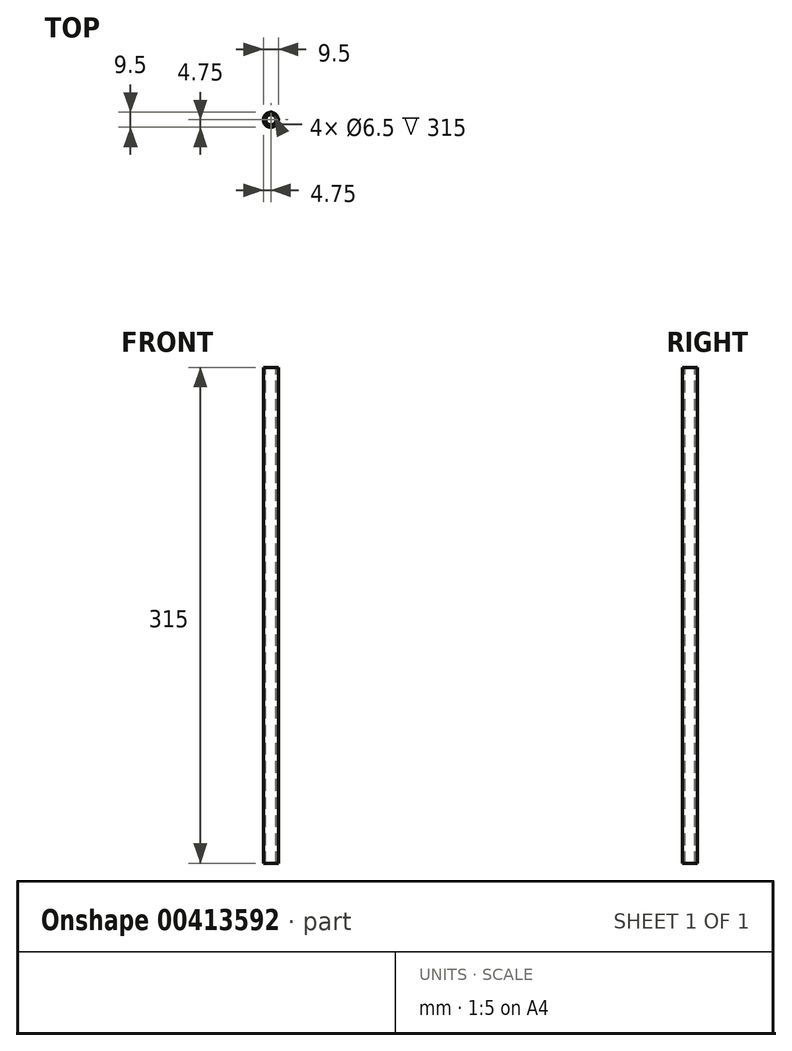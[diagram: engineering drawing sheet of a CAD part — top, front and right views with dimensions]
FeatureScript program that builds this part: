
annotation { "Feature Type Name" : "Feature", "Feature Type Description" : "" }
export const myFeature = defineFeature(function(context is Context, id is Id, definition is map)
    precondition{}
    {
        {
            var Q0;
            Q0=qCreatedBy(makeId("Front.planeOp"),FACE);
            var sketch = newSketch(context, id + "F0", { "sketchPlane" : qUnion([Q0])});
            skLineSegment(sketch, "E0.bottom", {"start": v(-3.25, -157.5) * mm, "end": v(-4.75, -157.5) * mm});
            skLineSegment(sketch, "E0.top", {"start": v(-3.25, 157.5) * mm, "end": v(-4.75, 157.5) * mm});
            skLineSegment(sketch, "E0.left", {"start": v(-3.25, -157.5) * mm, "end": v(-3.25, 157.5) * mm});
            skLineSegment(sketch, "E0.right", {"start": v(-4.75, -157.5) * mm, "end": v(-4.75, 157.5) * mm});
            skPoint(sketch, "E1", {"position": v(-3.25, 0) * mm});
            skLineSegment(sketch, "E2", {"start": v(0, 74.9) * mm, "end": v(0, 37.67) * mm, "construction": true});
            skSolve(sketch);
        }
        {
            var Q0;
            Q0=makeQuery(id+"F0.imprint","IMPRINT",FACE,{"disambiguationData":[TD([[makeQuery(id+"F0.imprint","IMPRINT",EDGE,{"derivedFrom":sQuery(id+"F0.wireOp",EDGE,"E0.bottom")}),-1.0]])]});
            var Q1;
            Q1=sQuery(id+"F0.wireOp",EDGE,"E2");
            revolve(context, id + "F1", {"entities" : qUnion([Q0]), "axis" : qUnion([Q1]), "revolveType" : RevolveType.FULL});
        }
    });
